# Revit family: FP-Revit18-RIV3-304-InductionCooker-0-CA-US-90000982A (1)
name_source: partatom
category: Specialty Equipment
units: mm (PartAtom-declared; Revit-internal decimal feet)

## family parameters
Always vertical = Yes
Cut with Voids When Loaded = Yes
OmniClass Number = 23.40.40.14.17.17
OmniClass Title = Ranges
Part Type = Normal
Room Calculation Point = No
Round Connector Dimension = Use Diameter
Shared = No
Work Plane-Based = No

## types (1)
- FP-Revit18-RIV3-304-InductionCooker-0-CA-US-90000982A (1)
    Cavity - Depth = 704 mm  [stored 2.30971 ft]
    Cavity - Height = 0 mm  [stored 0 ft]
    Cavity - Width = 765 mm  [stored 2.50984 ft]
    Clearance - Overhead Combustible = 1372 mm  [stored 4.50131 ft]
    Clearance - Overhead Non-Combustible = 762 mm  [stored 2.5 ft]
    Clearance - Overhead Rangehood = 915 mm  [stored 3.00197 ft]
    Clearance - Rear Combustible = 305 mm  [stored 1.00066 ft]
    Clearance - Rear Non-Combustible = 0 mm  [stored 0 ft]
    Clearance - Side Combustible = 305 mm  [stored 1.00066 ft]
    Clearance - Side Non-Combustible = 0 mm  [stored 0 ft]
    Connector Note - Electrical = 120/208 V or 120/240 V, 60Hz, 50 amp fused electrical supply, 57 amp Max
    Countertop Height (min 908mm - max 933mm) = 915 mm  [stored 3.00197 ft]
    Default Elevation = 0 mm  [stored 0 ft]
    Description = Induction Range, 30", 4 Zones with SmartZone
    Manufacturer = Fisher & Paykel Appliances
    Material - Body = Fisher & Paykel - Stainless Steel
    Material - Buttons and Dials = Fisher & Paykel - Aluminium, Dark
    Material - Display Panel = Fisher & Paykel - Black
    Material - Glass = Fisher & Paykel - Glass, Black
    Material - Handle = Fisher & Paykel - Stainless Steel
    Material - Trim = Fisher & Paykel - Aluminium
    Model = RIV3-304
    Product - Depth = 703 mm  [stored 2.30643 ft]
    Product - Height = 915 mm  [stored 3.00197 ft]
    Product - Width = 759 mm  [stored 2.49016 ft]
    URL = www.fisherpaykel.com
    Visibility - Clearance Required = Yes

note: [stored X ft] marks values corroborated as IEEE doubles in the binary element streams (Revit-internal decimal feet)

## geometry (parser evidence)
native form markers: Sweep x8
no freeform markers — native parametric forms only
